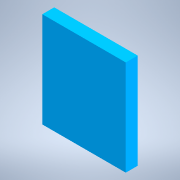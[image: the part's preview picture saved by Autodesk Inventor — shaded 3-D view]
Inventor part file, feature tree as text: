
AUTODESK INVENTOR PART (.ipt)
format: ipt  version: 2022.3 (Build 263350000, 350)  size: 100,352 bytes
history: native  units: in
note: dims shown in document units (in); Inventor stores cm internally (conversion verified against a paired STEP export)
features: extrude x1, sketch x1
ambient origin geometry x8: Origin, YZ Plane, XZ Plane, XY Plane, X Axis, Y Axis, Z Axis, Center Point
bodies: Solid1 (feature_tree)
feature tree (2):
  extrude  "Extrusion1"  Depth=0.8in
  sketch  "Sketch1"  dims[d0=0.7in d1=0.8in d2=0.1in d3=0.0in]
